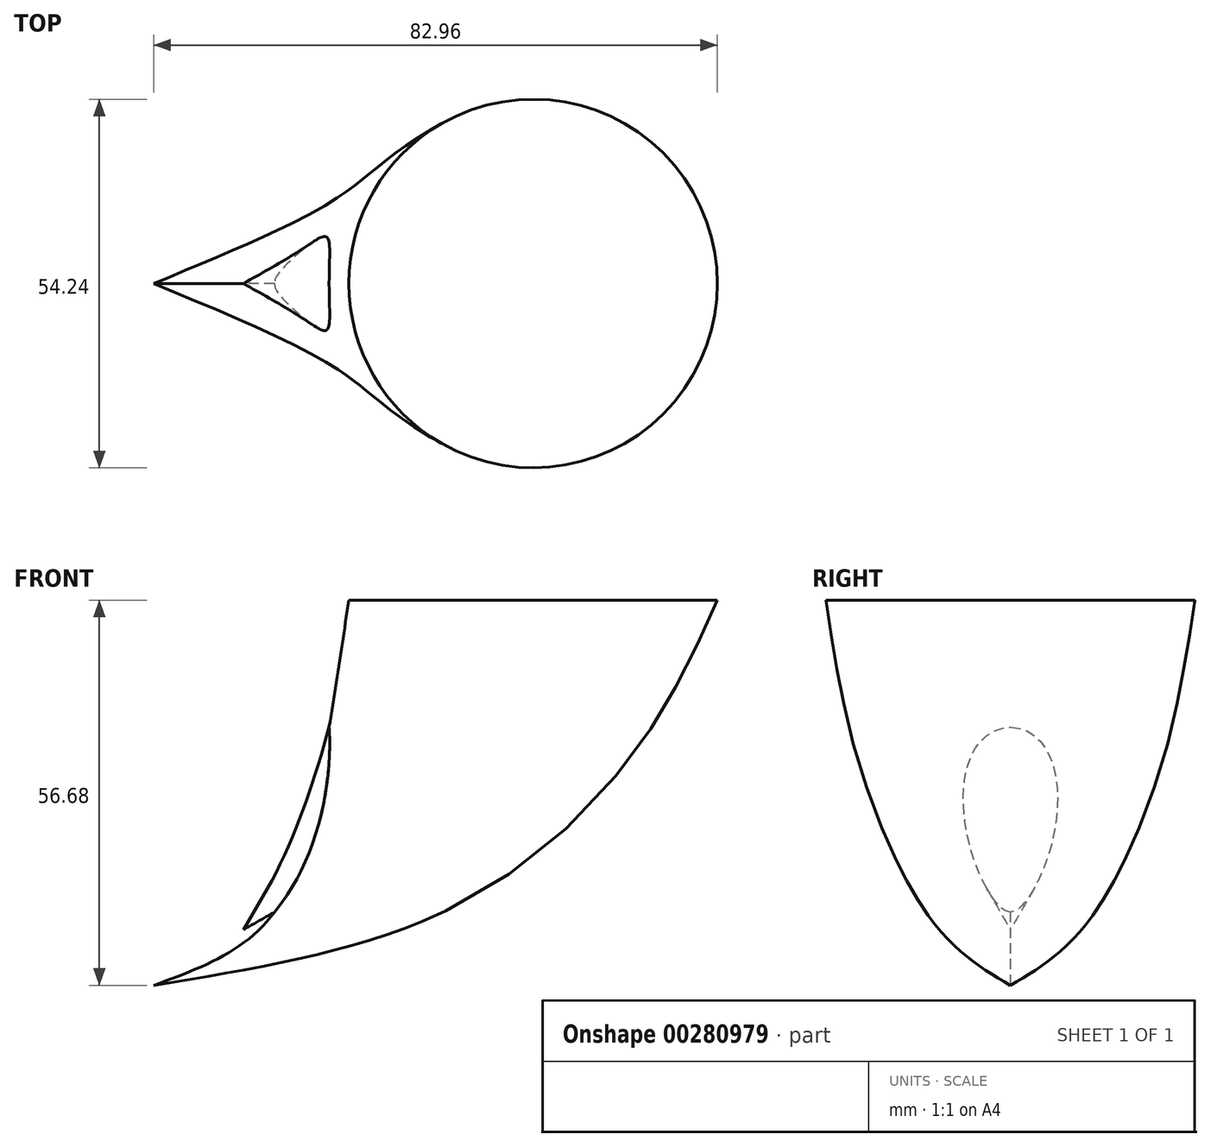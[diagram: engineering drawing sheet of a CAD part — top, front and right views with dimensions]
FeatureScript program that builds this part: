
annotation { "Feature Type Name" : "Feature", "Feature Type Description" : "" }
export const myFeature = defineFeature(function(context is Context, id is Id, definition is map)
    precondition{}
    {
        {
            var Q0;
            Q0=qCreatedBy(makeId("Top.planeOp"),FACE);
            cPlane(context, id + "F0", {"entities" : qUnion([Q0]), "cplaneType" : CPlaneType.OFFSET, "offset" : 14.7 * mm, "oppositeDirection" : true, "width" : 150 * mm, "height" : 150 * mm});
        }
        {
            var Q0;
            Q0=qCreatedBy(makeId("Top.planeOp"),FACE);
            cPlane(context, id + "F1", {"entities" : qUnion([Q0]), "cplaneType" : CPlaneType.OFFSET, "offset" : 28.9 * mm, "oppositeDirection" : true, "width" : 150 * mm, "height" : 150 * mm});
        }
        {
            var Q0;
            Q0=qCreatedBy(makeId("Top.planeOp"),FACE);
            cPlane(context, id + "F2", {"entities" : qUnion([Q0]), "cplaneType" : CPlaneType.OFFSET, "offset" : 75.4 * mm, "oppositeDirection" : true, "width" : 150 * mm, "height" : 150 * mm});
        }
        {
            var Q0;
            Q0=qCreatedBy(makeId("Right.planeOp"),FACE);
            cPlane(context, id + "F3", {"entities" : qUnion([Q0]), "cplaneType" : CPlaneType.OFFSET, "offset" : 26.4 * mm, "oppositeDirection" : true, "width" : 150 * mm, "height" : 150 * mm});
        }
        {
            var Q0;
            Q0=qCreatedBy(id+"F0.planeOp",FACE);
            var sketch = newSketch(context, id + "F4", { "sketchPlane" : qUnion([Q0])});
            skCircle(sketch, "E0", {"center": v(30.9, 0) * mm, "radius": 31 * mm});
            skSolve(sketch);
        }
        {
            var Q0;
            Q0=qCreatedBy(id+"F1.planeOp",FACE);
            var sketch = newSketch(context, id + "F5", { "sketchPlane" : qUnion([Q0])});
            skCircle(sketch, "E1", {"center": v(29.44, 0) * mm, "radius": 27.12 * mm});
            skSolve(sketch);
        }
        {
            var Q0;
            Q0=qCreatedBy(id+"F2.planeOp",FACE);
            var sketch = newSketch(context, id + "F6", { "sketchPlane" : qUnion([Q0])});
            skCircle(sketch, "E2", {"center": v(2.92, 0) * mm, "radius": 12.02 * mm});
            skSolve(sketch);
        }
        {
            var Q0;
            Q0=qCreatedBy(id+"F3.planeOp",FACE);
            var sketch = newSketch(context, id + "F7", { "sketchPlane" : qUnion([Q0])});
            skCircle(sketch, "E3", {"center": v(0, -85.58) * mm, "radius": 0.83 * mm});
            skSolve(sketch);
        }
        {
            var Q0;
            Q0=qCreatedBy(makeId("Top.planeOp"),FACE);
            cPlane(context, id + "F8", {"entities" : qUnion([Q0]), "cplaneType" : CPlaneType.OFFSET, "offset" : 77.4 * mm, "oppositeDirection" : true, "width" : 150 * mm, "height" : 150 * mm});
        }
        {
            var Q0;
            Q0=qCreatedBy(makeId("Top.planeOp"),FACE);
            cPlane(context, id + "F9", {"entities" : qUnion([Q0]), "cplaneType" : CPlaneType.OFFSET, "offset" : 69.5 * mm, "oppositeDirection" : true, "width" : 150 * mm, "height" : 150 * mm});
        }
        {
            var Q0;
            Q0=qCreatedBy(id+"F8.planeOp",FACE);
            var sketch = newSketch(context, id + "F10", { "sketchPlane" : qUnion([Q0])});
            skCircle(sketch, "E4", {"center": v(-13.2, 0) * mm, "radius": 0.24 * mm});
            skSolve(sketch);
        }
        {
            var Q0;
            Q0=qCreatedBy(id+"F9.planeOp",FACE);
            var sketch = newSketch(context, id + "F11", { "sketchPlane" : qUnion([Q0])});
            skCircle(sketch, "E5", {"center": v(-4.17, 0) * mm, "radius": 4.5 * mm});
            skSolve(sketch);
        }
        {
            var Q0;
            Q0=qCreatedBy(makeId("Top.planeOp"),FACE);
            cPlane(context, id + "F12", {"entities" : qUnion([Q0]), "cplaneType" : CPlaneType.OFFSET, "offset" : 51.4 * mm, "oppositeDirection" : true, "width" : 150 * mm, "height" : 150 * mm});
        }
        {
            var Q0;
            Q0=qCreatedBy(id+"F12.planeOp",FACE);
            var sketch = newSketch(context, id + "F13", { "sketchPlane" : qUnion([Q0])});
            skCircle(sketch, "E6", {"center": v(21.52, 0) * mm, "radius": 22.74 * mm});
            skSolve(sketch);
        }
        {
            var Q0;
            Q0=makeQuery(id+"F5.imprint","IMPRINT",FACE,{"disambiguationData":[TD([[makeQuery(id+"F5.imprint","IMPRINT",EDGE,{"derivedFrom":sQuery(id+"F5.wireOp",EDGE,"E1")}),1.0]])]});
            var Q1;
            Q1=makeQuery(id+"F13.imprint","IMPRINT",FACE,{"disambiguationData":[TD([[makeQuery(id+"F13.imprint","IMPRINT",EDGE,{"derivedFrom":sQuery(id+"F13.wireOp",EDGE,"E6")}),1.0]])]});
            var Q2;
            Q2=makeQuery(id+"F6.imprint","IMPRINT",FACE,{"disambiguationData":[TD([[makeQuery(id+"F6.imprint","IMPRINT",EDGE,{"derivedFrom":sQuery(id+"F6.wireOp",EDGE,"E2")}),1.0]])]});
            var Q3;
            Q3=sQuery(id+"F7.wireOp",VERTEX,"E3.center");
            var Q4;
            Q4=makeQuery(id+"F4.imprint","IMPRINT",FACE,{"disambiguationData":[TD([[makeQuery(id+"F4.imprint","IMPRINT",EDGE,{"derivedFrom":sQuery(id+"F4.wireOp",EDGE,"E0")}),1.0]])]});
            var Q5;
            Q5=makeQuery(id+"F5.imprint","IMPRINT",FACE,{"disambiguationData":[TD([[makeQuery(id+"F5.imprint","IMPRINT",EDGE,{"derivedFrom":sQuery(id+"F5.wireOp",EDGE,"E1")}),1.0]])]});
            var Q6;
            Q6=makeQuery(id+"F13.imprint","IMPRINT",FACE,{"disambiguationData":[TD([[makeQuery(id+"F13.imprint","IMPRINT",EDGE,{"derivedFrom":sQuery(id+"F13.wireOp",EDGE,"E6")}),1.0]])]});
            var Q7;
            Q7=makeQuery(id+"F6.imprint","IMPRINT",FACE,{"disambiguationData":[TD([[makeQuery(id+"F6.imprint","IMPRINT",EDGE,{"derivedFrom":sQuery(id+"F6.wireOp",EDGE,"E2")}),1.0]])]});
            var Q8;
            Q8=sQuery(id+"F7.wireOp",VERTEX,"E3.center");
            loft(context, id + "F14", {"sheetProfilesArray" : [{ "sheetProfileEntities" : qUnion([Q0]) }, { "sheetProfileEntities" : qUnion([Q1]) }, { "sheetProfileEntities" : qUnion([Q2]) }, { "sheetProfileEntities" : qUnion([Q3]) }], "wireProfilesArray" : [{ "wireProfileEntities" : qUnion([Q4]) }, { "wireProfileEntities" : qUnion([Q5]) }, { "wireProfileEntities" : qUnion([Q6]) }, { "wireProfileEntities" : qUnion([Q7]) }, { "wireProfileEntities" : qUnion([Q8]) }]});
        }
        {
            var Q0;
            Q0=makeQuery(id+"F5.imprint","IMPRINT",FACE,{"disambiguationData":[TD([[makeQuery(id+"F5.imprint","IMPRINT",EDGE,{"derivedFrom":sQuery(id+"F5.wireOp",EDGE,"E1")}),1.0]])]});
            cPlane(context, id + "F15", {"entities" : qUnion([Q0]), "cplaneType" : CPlaneType.OFFSET, "offset" : 9.7 * mm, "oppositeDirection" : true, "width" : 150 * mm, "height" : 150 * mm});
        }
        {
            var Q0;
            Q0=qCreatedBy(id+"F15.planeOp",FACE);
            var sketch = newSketch(context, id + "F16", { "sketchPlane" : qUnion([Q0])});
            skCircle(sketch, "E7", {"center": v(22.3, 0) * mm, "radius": 20.48 * mm});
            skSolve(sketch);
        }
        {
            var Q0;
            Q0=sQuery(id+"F10.wireOp",VERTEX,"E4.center");
            var Q1;
            Q1=makeQuery(id+"F11.imprint","IMPRINT",FACE,{"disambiguationData":[TD([[makeQuery(id+"F11.imprint","IMPRINT",EDGE,{"derivedFrom":sQuery(id+"F11.wireOp",EDGE,"E5")}),1.0]])]});
            var Q2;
            Q2 = qSketchRegion(id + "F16", true);
            loft(context, id + "F17", {"operationType" : NewBodyOperationType.ADD, "sheetProfilesArray" : [{ "sheetProfileEntities" : qUnion([Q0]) }, { "sheetProfileEntities" : qUnion([Q1]) }, { "sheetProfileEntities" : qUnion([Q2]) }]});
        }
    });
